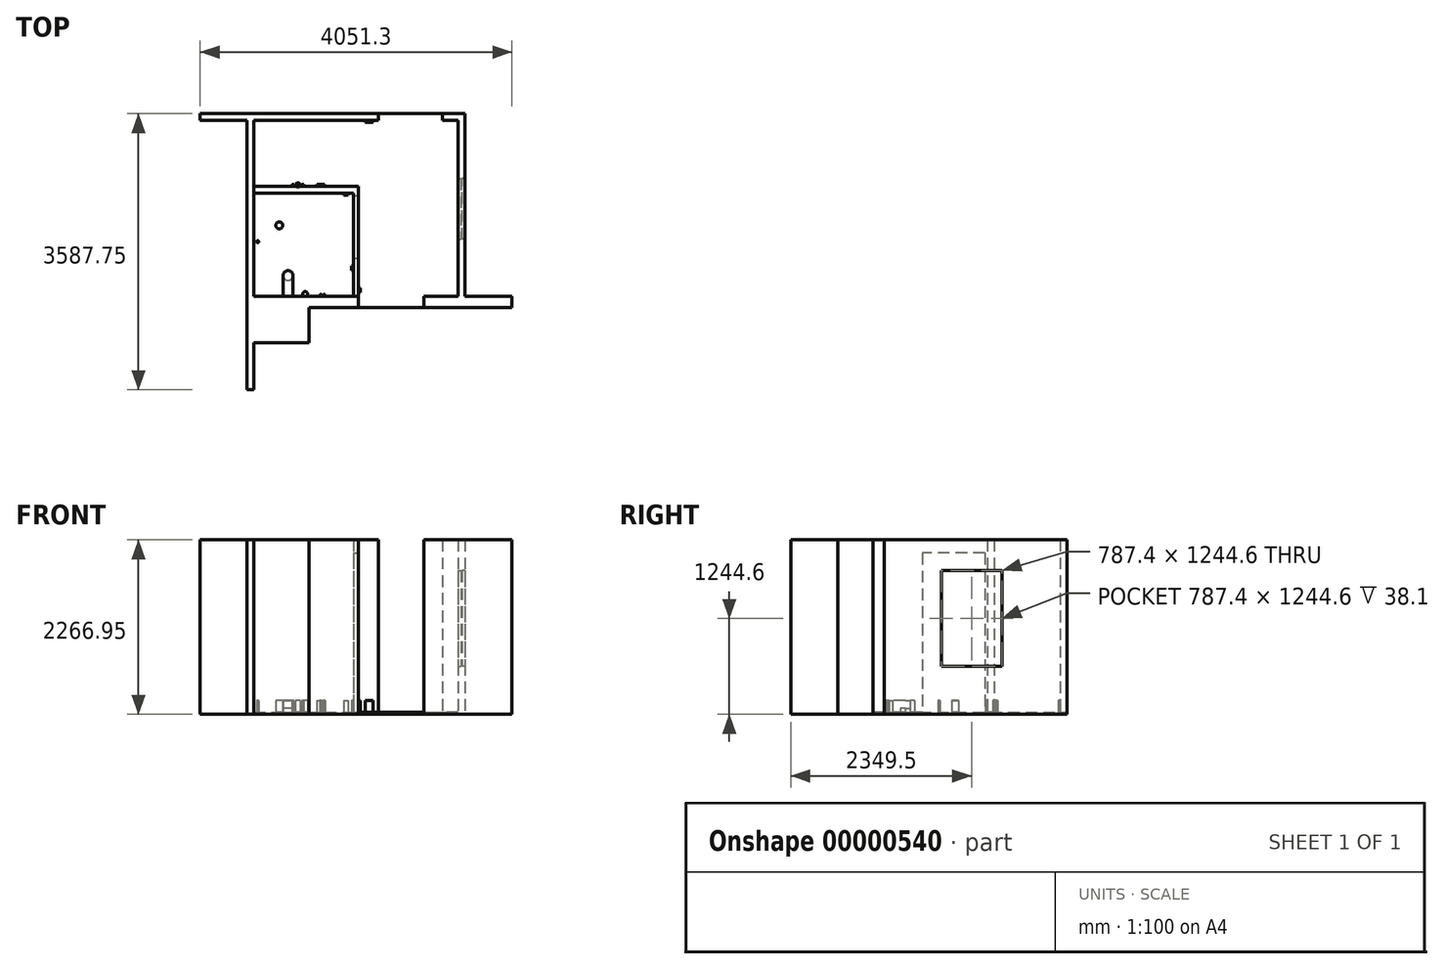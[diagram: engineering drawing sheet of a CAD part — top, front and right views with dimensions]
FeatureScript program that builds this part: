
annotation { "Feature Type Name" : "Feature", "Feature Type Description" : "" }
export const myFeature = defineFeature(function(context is Context, id is Id, definition is map)
    precondition{}
    {
        {
            var Q0;
            Q0=qCreatedBy(makeId("Top.planeOp"),FACE);
            var sketch = newSketch(context, id + "F0", { "sketchPlane" : qUnion([Q0])});
            skLineSegment(sketch, "E0.bottom", {"start": v(0, 2286) * mm, "end": v(1619.25, 2286) * mm});
            skLineSegment(sketch, "E0.top", {"start": v(0, 0) * mm, "end": v(1358.9, 0) * mm});
            skLineSegment(sketch, "E0.left", {"start": v(0, 2286) * mm, "end": v(0, 0) * mm});
            skLineSegment(sketch, "E1", {"start": v(1358.9, 0) * mm, "end": v(1358.9, -146.05) * mm});
            skLineSegment(sketch, "E2", {"start": v(1358.9, -146.05) * mm, "end": v(717.55, -146.05) * mm});
            skLineSegment(sketch, "E3", {"start": v(717.55, -146.05) * mm, "end": v(717.55, -603.25) * mm});
            skLineSegment(sketch, "E4", {"start": v(717.55, -603.25) * mm, "end": v(0, -603.25) * mm});
            skLineSegment(sketch, "E5", {"start": v(0, -603.25) * mm, "end": v(0, -1212.85) * mm});
            skLineSegment(sketch, "E6", {"start": v(2209.8, -146.05) * mm, "end": v(2209.8, 0) * mm});
            skLineSegment(sketch, "E7", {"start": v(2209.8, 0) * mm, "end": v(2654.3, 0) * mm});
            skLineSegment(sketch, "E8", {"start": v(2654.3, 0) * mm, "end": v(2654.3, 2286) * mm});
            skLineSegment(sketch, "E9", {"start": v(2654.3, 2286) * mm, "end": v(2451.1, 2286) * mm});
            skLineSegment(sketch, "E10", {"start": v(2451.1, 2286) * mm, "end": v(2451.1, 2374.9) * mm});
            skLineSegment(sketch, "E11", {"start": v(2451.1, 2374.9) * mm, "end": v(2743.2, 2374.9) * mm});
            skLineSegment(sketch, "E12", {"start": v(2743.2, 2374.9) * mm, "end": v(2743.2, 0) * mm});
            skLineSegment(sketch, "E13", {"start": v(2743.2, 0) * mm, "end": v(3352.8, 0) * mm});
            skLineSegment(sketch, "E14", {"start": v(1619.25, 2286) * mm, "end": v(1619.25, 2374.9) * mm});
            skLineSegment(sketch, "E15", {"start": v(1619.25, 2374.9) * mm, "end": v(-698.5, 2374.9) * mm});
            skLineSegment(sketch, "E16", {"start": v(-698.5, 2374.9) * mm, "end": v(-698.5, 2286) * mm});
            skLineSegment(sketch, "E17", {"start": v(-698.5, 2286) * mm, "end": v(-88.9, 2286) * mm});
            skLineSegment(sketch, "E18", {"start": v(-88.9, 2286) * mm, "end": v(-88.9, -1212.85) * mm});
            skLineSegment(sketch, "E19", {"start": v(2209.8, -146.05) * mm, "end": v(3352.8, -146.05) * mm});
            skLineSegment(sketch, "E20", {"start": v(3352.8, -146.05) * mm, "end": v(3352.8, 0) * mm});
            skLineSegment(sketch, "E21", {"start": v(-88.9, -1212.85) * mm, "end": v(0, -1212.85) * mm});
            skSolve(sketch);
        }
        {
            var Q0;
            Q0 = qSketchRegion(id + "F0", true);
            extrude(context, id + "F1", {"entities" : qUnion([Q0]), "depth" : 2241.55 * mm, "offsetDistance" : 25.4 * mm});
        }
        {
            var Q0;
            Q0=qCreatedBy(makeId("Top.planeOp"),FACE);
            var sketch = newSketch(context, id + "F2", { "sketchPlane" : qUnion([Q0])});
            skLineSegment(sketch, "E22.0", {"start": v(2743.2, 0) * mm, "end": v(3352.8, 0) * mm});
            skLineSegment(sketch, "E22.1", {"start": v(2743.2, 2374.9) * mm, "end": v(2743.2, 0) * mm});
            skLineSegment(sketch, "E22.2", {"start": v(2451.1, 2374.9) * mm, "end": v(2743.2, 2374.9) * mm});
            skLineSegment(sketch, "E22.3", {"start": v(-698.5, 2374.9) * mm, "end": v(-698.5, 2286) * mm});
            skLineSegment(sketch, "E22.4", {"start": v(-698.5, 2286) * mm, "end": v(-88.9, 2286) * mm});
            skLineSegment(sketch, "E22.5", {"start": v(-88.9, 2286) * mm, "end": v(-88.9, -1212.85) * mm});
            skLineSegment(sketch, "E23", {"start": v(-698.5, 2374.9) * mm, "end": v(2451.1, 2374.9) * mm});
            skLineSegment(sketch, "E24", {"start": v(-88.9, -1212.85) * mm, "end": v(0, -1212.85) * mm});
            skLineSegment(sketch, "E25", {"start": v(0, -1212.85) * mm, "end": v(0, -603.25) * mm});
            skLineSegment(sketch, "E26", {"start": v(0, -603.25) * mm, "end": v(717.55, -603.25) * mm});
            skLineSegment(sketch, "E27", {"start": v(717.55, -603.25) * mm, "end": v(717.55, -146.05) * mm});
            skLineSegment(sketch, "E28", {"start": v(717.55, -146.05) * mm, "end": v(3352.8, -146.05) * mm});
            skLineSegment(sketch, "E29", {"start": v(3352.8, -146.05) * mm, "end": v(3352.8, 0) * mm});
            skSolve(sketch);
        }
        {
            var Q0;
            Q0 = qSketchRegion(id + "F2", true);
            extrude(context, id + "F3", {"entities" : qUnion([Q0]), "oppositeDirection" : true, "depth" : 25.4 * mm, "offsetDistance" : 25.4 * mm});
        }
        {
            var Q0;
            Q0=makeQuery(id+"F1.opExtrude","SWEPT_BODY",BODY,{"disambiguationData":[OSD([sQuery(id+"F0.wireOp",EDGE,"E0.bottom"),sQuery(id+"F0.wireOp",EDGE,"E0.top"),sQuery(id+"F0.wireOp",EDGE,"E0.left"),sQuery(id+"F0.wireOp",EDGE,"E1"),sQuery(id+"F0.wireOp",EDGE,"E2"),sQuery(id+"F0.wireOp",EDGE,"E3"),sQuery(id+"F0.wireOp",EDGE,"E4"),sQuery(id+"F0.wireOp",EDGE,"E5"),sQuery(id+"F0.wireOp",EDGE,"E14"),sQuery(id+"F0.wireOp",EDGE,"E15"),sQuery(id+"F0.wireOp",EDGE,"E16"),sQuery(id+"F0.wireOp",EDGE,"E17"),sQuery(id+"F0.wireOp",EDGE,"E18"),sQuery(id+"F0.wireOp",EDGE,"E21")])]});
            var Q1;
            Q1=makeQuery(id+"F1.opExtrude","SWEPT_BODY",BODY,{"disambiguationData":[OSD([sQuery(id+"F0.wireOp",EDGE,"E6"),sQuery(id+"F0.wireOp",EDGE,"E7"),sQuery(id+"F0.wireOp",EDGE,"E8"),sQuery(id+"F0.wireOp",EDGE,"E9"),sQuery(id+"F0.wireOp",EDGE,"E10"),sQuery(id+"F0.wireOp",EDGE,"E11"),sQuery(id+"F0.wireOp",EDGE,"E12"),sQuery(id+"F0.wireOp",EDGE,"E13"),sQuery(id+"F0.wireOp",EDGE,"E19"),sQuery(id+"F0.wireOp",EDGE,"E20")])]});
            var Q2;
            Q2=makeQuery(id+"F3.opExtrude","SWEPT_BODY",BODY,{"disambiguationData":[OSD([sQuery(id+"F2.wireOp",EDGE,"0252bfec-053e-4e23-b52a-fb082310881f"),sQuery(id+"F2.wireOp",EDGE,"E22.0"),sQuery(id+"F2.wireOp",EDGE,"E22.1"),sQuery(id+"F2.wireOp",EDGE,"E22.2"),sQuery(id+"F2.wireOp",EDGE,"E22.3"),sQuery(id+"F2.wireOp",EDGE,"E22.4"),sQuery(id+"F2.wireOp",EDGE,"E22.5"),sQuery(id+"F2.wireOp",EDGE,"E23")])]});
            booleanBodies(context, id + "F4", {"operationType" : BooleanOperationType.UNION, "tools" : qUnion([Q0, Q1, Q2])});
        }
        {
            var Q0;
            Q0=qCreatedBy(makeId("Top.planeOp"),FACE);
            cPlane(context, id + "F5", {"entities" : qUnion([Q0]), "cplaneType" : CPlaneType.OFFSET, "offset" : 596.9 * mm, "width" : 152.4 * mm, "height" : 152.4 * mm});
        }
        {
            var Q0;
            Q0=qCreatedBy(id+"F5.planeOp",FACE);
            var sketch = newSketch(context, id + "F6", { "sketchPlane" : qUnion([Q0])});
            skLineSegment(sketch, "E30.bottom", {"start": v(2654.3, 1530.35) * mm, "end": v(2692.4, 1530.35) * mm});
            skLineSegment(sketch, "E30.top", {"start": v(2654.3, 742.95) * mm, "end": v(2692.4, 742.95) * mm});
            skLineSegment(sketch, "E30.left", {"start": v(2654.3, 1530.35) * mm, "end": v(2654.3, 742.95) * mm});
            skLineSegment(sketch, "E30.right", {"start": v(2692.4, 1530.35) * mm, "end": v(2692.4, 742.95) * mm});
            skLineSegment(sketch, "E31.bottom", {"start": v(2743.2, 742.95) * mm, "end": v(2705.1, 742.95) * mm});
            skLineSegment(sketch, "E31.top", {"start": v(2743.2, 1530.35) * mm, "end": v(2705.1, 1530.35) * mm});
            skLineSegment(sketch, "E31.left", {"start": v(2743.2, 742.95) * mm, "end": v(2743.2, 1530.35) * mm});
            skLineSegment(sketch, "E31.right", {"start": v(2705.1, 742.95) * mm, "end": v(2705.1, 1530.35) * mm});
            skSolve(sketch);
        }
        {
            var Q0;
            Q0 = qSketchRegion(id + "F6", true);
            extrude(context, id + "F7", {"entities" : qUnion([Q0]), "operationType" : NewBodyOperationType.REMOVE, "depth" : 1244.6 * mm, "offsetDistance" : 25.4 * mm});
        }
        {
            var Q0;
            Q0=makeQuery(id+"F3.opExtrude","CAP_FACE",FACE,{"disambiguationData":[OSD([sQuery(id+"F2.wireOp",EDGE,"0252bfec-053e-4e23-b52a-fb082310881f"),sQuery(id+"F2.wireOp",EDGE,"E22.0"),sQuery(id+"F2.wireOp",EDGE,"E22.1"),sQuery(id+"F2.wireOp",EDGE,"E22.2"),sQuery(id+"F2.wireOp",EDGE,"E22.3"),sQuery(id+"F2.wireOp",EDGE,"E22.4"),sQuery(id+"F2.wireOp",EDGE,"E22.5"),sQuery(id+"F2.wireOp",EDGE,"E23")])],"isStart":true});
            var sketch = newSketch(context, id + "F8", { "sketchPlane" : qUnion([Q0])});
            skLineSegment(sketch, "E32", {"start": v(1358.9, 0) * mm, "end": v(1358.9, 1431.93) * mm});
            skLineSegment(sketch, "E33", {"start": v(1358.9, 1431.93) * mm, "end": v(0, 1431.93) * mm});
            skLineSegment(sketch, "E34", {"start": v(0, 1431.93) * mm, "end": v(0, 1343.02) * mm});
            skLineSegment(sketch, "E35", {"start": v(0, 1343.02) * mm, "end": v(1295.4, 1343.03) * mm});
            skLineSegment(sketch, "E36", {"start": v(1295.4, 1343.03) * mm, "end": v(1295.4, 0) * mm});
            skLineSegment(sketch, "E37", {"start": v(1295.4, 0) * mm, "end": v(1358.9, 0) * mm});
            skSolve(sketch);
        }
        {
            var Q0;
            Q0 = qSketchRegion(id + "F8", true);
            var Q1;
            Q1=makeQuery(id+"F1.opExtrude","CAP_FACE",FACE,{"disambiguationData":[OSD([sQuery(id+"F0.wireOp",EDGE,"E0.bottom"),sQuery(id+"F0.wireOp",EDGE,"E0.top"),sQuery(id+"F0.wireOp",EDGE,"E0.left"),sQuery(id+"F0.wireOp",EDGE,"E1"),sQuery(id+"F0.wireOp",EDGE,"E2"),sQuery(id+"F0.wireOp",EDGE,"E3"),sQuery(id+"F0.wireOp",EDGE,"E4"),sQuery(id+"F0.wireOp",EDGE,"E5"),sQuery(id+"F0.wireOp",EDGE,"E14"),sQuery(id+"F0.wireOp",EDGE,"E15"),sQuery(id+"F0.wireOp",EDGE,"E16"),sQuery(id+"F0.wireOp",EDGE,"E17"),sQuery(id+"F0.wireOp",EDGE,"E18"),sQuery(id+"F0.wireOp",EDGE,"E21")])],"isStart":false});
            extrude(context, id + "F9", {"entities" : qUnion([Q0]), "endBound" : BoundingType.UP_TO_SURFACE, "depth" : 25.4 * mm, "endBoundEntityFace" : qUnion([Q1]), "offsetDistance" : 25.4 * mm});
        }
        {
            var Q0;
            Q0=makeQuery(id+"F9.opExtrude","SWEPT_FACE",FACE,{"disambiguationData":[OSD([sQuery(id+"F8.wireOp",EDGE,"E32")])]});
            var sketch = newSketch(context, id + "F10", { "sketchPlane" : qUnion([Q0])});
            skLineSegment(sketch, "E38.bottom", {"start": v(495.3, 0) * mm, "end": v(1308.1, 0) * mm});
            skLineSegment(sketch, "E38.top", {"start": v(495.3, 2070.1) * mm, "end": v(1308.1, 2070.1) * mm});
            skLineSegment(sketch, "E38.left", {"start": v(495.3, 0) * mm, "end": v(495.3, 2070.1) * mm});
            skLineSegment(sketch, "E38.right", {"start": v(1308.1, 0) * mm, "end": v(1308.1, 2070.1) * mm});
            skSolve(sketch);
        }
        {
            var Q0;
            Q0 = qSketchRegion(id + "F10", true);
            var Q1;
            Q1=makeQuery(id+"F9.opExtrude","SWEPT_FACE",FACE,{"disambiguationData":[OSD([sQuery(id+"F8.wireOp",EDGE,"E36")])]});
            extrude(context, id + "F11", {"entities" : qUnion([Q0]), "operationType" : NewBodyOperationType.REMOVE, "endBound" : BoundingType.UP_TO_SURFACE, "oppositeDirection" : true, "depth" : 25.4 * mm, "endBoundEntityFace" : qUnion([Q1]), "offsetDistance" : 25.4 * mm});
        }
        {
            var Q0;
            Q0=makeQuery(id+"F3.opExtrude","CAP_FACE",FACE,{"disambiguationData":[OSD([sQuery(id+"F2.wireOp",EDGE,"0252bfec-053e-4e23-b52a-fb082310881f"),sQuery(id+"F2.wireOp",EDGE,"E22.0"),sQuery(id+"F2.wireOp",EDGE,"E22.1"),sQuery(id+"F2.wireOp",EDGE,"E22.2"),sQuery(id+"F2.wireOp",EDGE,"E22.3"),sQuery(id+"F2.wireOp",EDGE,"E22.4"),sQuery(id+"F2.wireOp",EDGE,"E22.5"),sQuery(id+"F2.wireOp",EDGE,"E23")])],"isStart":true});
            var sketch = newSketch(context, id + "F12", { "sketchPlane" : qUnion([Q0])});
            skLineSegment(sketch, "E39.bottom", {"start": v(819.15, 1431.93) * mm, "end": v(920.75, 1431.93) * mm});
            skLineSegment(sketch, "E39.top", {"start": v(819.15, 1457.33) * mm, "end": v(920.75, 1457.33) * mm});
            skLineSegment(sketch, "E39.left", {"start": v(819.15, 1431.93) * mm, "end": v(819.15, 1457.33) * mm});
            skLineSegment(sketch, "E39.right", {"start": v(920.75, 1431.93) * mm, "end": v(920.75, 1457.33) * mm});
            skLineSegment(sketch, "E40.bottom", {"start": v(1165.22, 1343.03) * mm, "end": v(1222.38, 1343.03) * mm});
            skLineSegment(sketch, "E40.top", {"start": v(1165.22, 1317.63) * mm, "end": v(1222.38, 1317.63) * mm});
            skLineSegment(sketch, "E40.left", {"start": v(1165.22, 1343.03) * mm, "end": v(1165.22, 1317.63) * mm});
            skLineSegment(sketch, "E40.right", {"start": v(1222.38, 1343.03) * mm, "end": v(1222.38, 1317.63) * mm});
            skLineSegment(sketch, "E41.bottom", {"start": v(1358.9, 50.8) * mm, "end": v(1384.3, 50.8) * mm});
            skLineSegment(sketch, "E41.top", {"start": v(1358.9, 107.95) * mm, "end": v(1384.3, 107.95) * mm});
            skLineSegment(sketch, "E41.left", {"start": v(1358.9, 50.8) * mm, "end": v(1358.9, 107.95) * mm});
            skLineSegment(sketch, "E41.right", {"start": v(1384.3, 50.8) * mm, "end": v(1384.3, 107.95) * mm});
            skLineSegment(sketch, "E42.bottom", {"start": v(1295.4, 393.7) * mm, "end": v(1270, 393.7) * mm});
            skLineSegment(sketch, "E42.top", {"start": v(1295.4, 336.55) * mm, "end": v(1270, 336.55) * mm});
            skLineSegment(sketch, "E42.left", {"start": v(1295.4, 393.7) * mm, "end": v(1295.4, 336.55) * mm});
            skLineSegment(sketch, "E42.right", {"start": v(1270, 393.7) * mm, "end": v(1270, 336.55) * mm});
            skCircle(sketch, "E43", {"center": v(571.5, 1444.62) * mm, "radius": 31.75 * mm});
            skCircle(sketch, "E44", {"center": v(635, 1444.62) * mm, "radius": 12.7 * mm});
            skCircle(sketch, "E45", {"center": v(508, 1444.62) * mm, "radius": 12.7 * mm});
            skCircle(sketch, "E46", {"center": v(330.2, 923.92) * mm, "radius": 44.45 * mm});
            skCircle(sketch, "E47", {"center": v(666.75, 31.75) * mm, "radius": 31.75 * mm});
            skCircle(sketch, "E48", {"center": v(869.95, 12.7) * mm, "radius": 12.7 * mm});
            skCircle(sketch, "E49", {"center": v(914.4, 12.7) * mm, "radius": 12.7 * mm});
            skLineSegment(sketch, "E50.bottom", {"start": v(1444.62, 2286) * mm, "end": v(1546.22, 2286) * mm});
            skLineSegment(sketch, "E50.top", {"start": v(1444.62, 2260.6) * mm, "end": v(1546.22, 2260.6) * mm});
            skLineSegment(sketch, "E50.left", {"start": v(1444.62, 2286) * mm, "end": v(1444.62, 2260.6) * mm});
            skLineSegment(sketch, "E50.right", {"start": v(1546.22, 2286) * mm, "end": v(1546.22, 2260.6) * mm});
            skCircle(sketch, "E51", {"center": v(444.5, 273.05) * mm, "radius": 63.5 * mm});
            skLineSegment(sketch, "E52.bottom", {"start": v(381, 273.05) * mm, "end": v(508, 273.05) * mm});
            skLineSegment(sketch, "E52.top", {"start": v(381, 0) * mm, "end": v(508, 0) * mm});
            skLineSegment(sketch, "E52.left", {"start": v(381, 273.05) * mm, "end": v(381, 0) * mm});
            skLineSegment(sketch, "E52.right", {"start": v(508, 273.05) * mm, "end": v(508, 0) * mm});
            skLineSegment(sketch, "E53.bottom", {"start": v(819.15, 1457.33) * mm, "end": v(876.3, 1457.33) * mm});
            skLineSegment(sketch, "E53.top", {"start": v(819.15, 1431.93) * mm, "end": v(876.3, 1431.93) * mm});
            skLineSegment(sketch, "E53.left", {"start": v(819.15, 1457.33) * mm, "end": v(819.15, 1431.93) * mm});
            skLineSegment(sketch, "E53.right", {"start": v(876.3, 1457.33) * mm, "end": v(876.3, 1431.93) * mm});
            skCircle(sketch, "E54", {"center": v(50.8, 711.2) * mm, "radius": 12.7 * mm});
            skSolve(sketch);
        }
        {
            var Q0;
            Q0 = qSketchRegion(id + "F12", true);
            var Q1;
            Q1 = qSketchRegion(id + "F12", true);
            var Q2;
            Q2 = qSketchRegion(id + "F12", true);
            extrude(context, id + "F13", {"entities" : qUnion([Q0, Q1, Q2]), "depth" : 152.4 * mm, "offsetDistance" : 25.4 * mm});
        }
        {
            var Q0;
            {var subQ0=sQuery(id+"F12.wireOp",EDGE,"E52.bottom");Q0=makeQuery(id+"F12.imprint","IMPRINT",FACE,{"disambiguationData":[TD([[makeQuery(id+"F12.imprint","IMPRINT",EDGE,{"derivedFrom":subQ0}),-1.0]])]});}
            var Q1;
            {var subQ0=sQuery(id+"F12.wireOp",EDGE,"E52.bottom");Q1=makeQuery(id+"F12.imprint","IMPRINT",FACE,{"disambiguationData":[TD([[makeQuery(id+"F12.imprint","IMPRINT",EDGE,{"derivedFrom":subQ0}),1.0]])]});}
            extrude(context, id + "F14", {"entities" : qUnion([Q0, Q1]), "operationType" : NewBodyOperationType.REMOVE, "depth" : 50.8 * mm, "offsetDistance" : 25.4 * mm});
        }
    });
